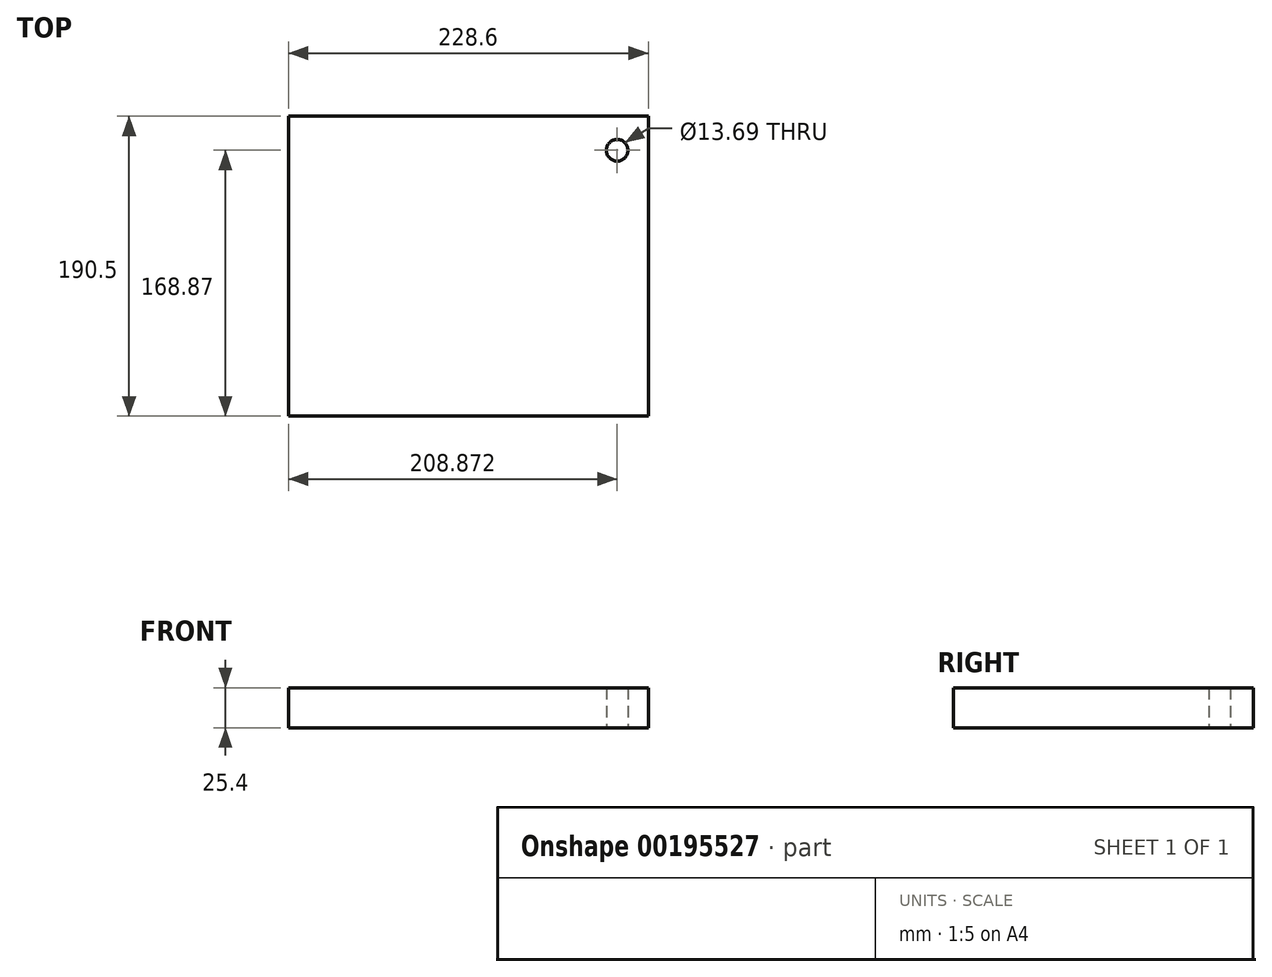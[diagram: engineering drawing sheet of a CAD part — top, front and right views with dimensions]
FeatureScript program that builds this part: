
annotation { "Feature Type Name" : "Feature", "Feature Type Description" : "" }
export const myFeature = defineFeature(function(context is Context, id is Id, definition is map)
    precondition{}
    {
        {
            var Q0;
            Q0=qCreatedBy(makeId("Top.planeOp"),FACE);
            var sketch = newSketch(context, id + "F0", { "sketchPlane" : qUnion([Q0])});
            skLineSegment(sketch, "E0.bottom", {"start": v(25.96, -44.65) * mm, "end": v(-202.64, -44.65) * mm});
            skLineSegment(sketch, "E0.top", {"start": v(25.96, 145.85) * mm, "end": v(-202.64, 145.85) * mm});
            skLineSegment(sketch, "E0.left", {"start": v(25.96, -44.65) * mm, "end": v(25.96, 145.85) * mm});
            skLineSegment(sketch, "E0.right", {"start": v(-202.64, -44.65) * mm, "end": v(-202.64, 145.85) * mm});
            skPoint(sketch, "E0.middle", {"position": v(-88.34, 50.6) * mm});
            skLineSegment(sketch, "E1", {"start": v(6.23, 124.22) * mm, "end": v(9.27, -44.65) * mm});
            skLineSegment(sketch, "E2", {"start": v(6.23, 124.22) * mm, "end": v(25.96, 124.22) * mm});
            skCircle(sketch, "E3", {"center": v(6.23, 124.22) * mm, "radius": 6.85 * mm});
            skSolve(sketch);
        }
        {
            var Q0;
            Q0 = qSketchRegion(id + "F0", true);
            extrude(context, id + "F1", {"entities" : qUnion([Q0]), "depth" : 25.4 * mm});
        }
    });
